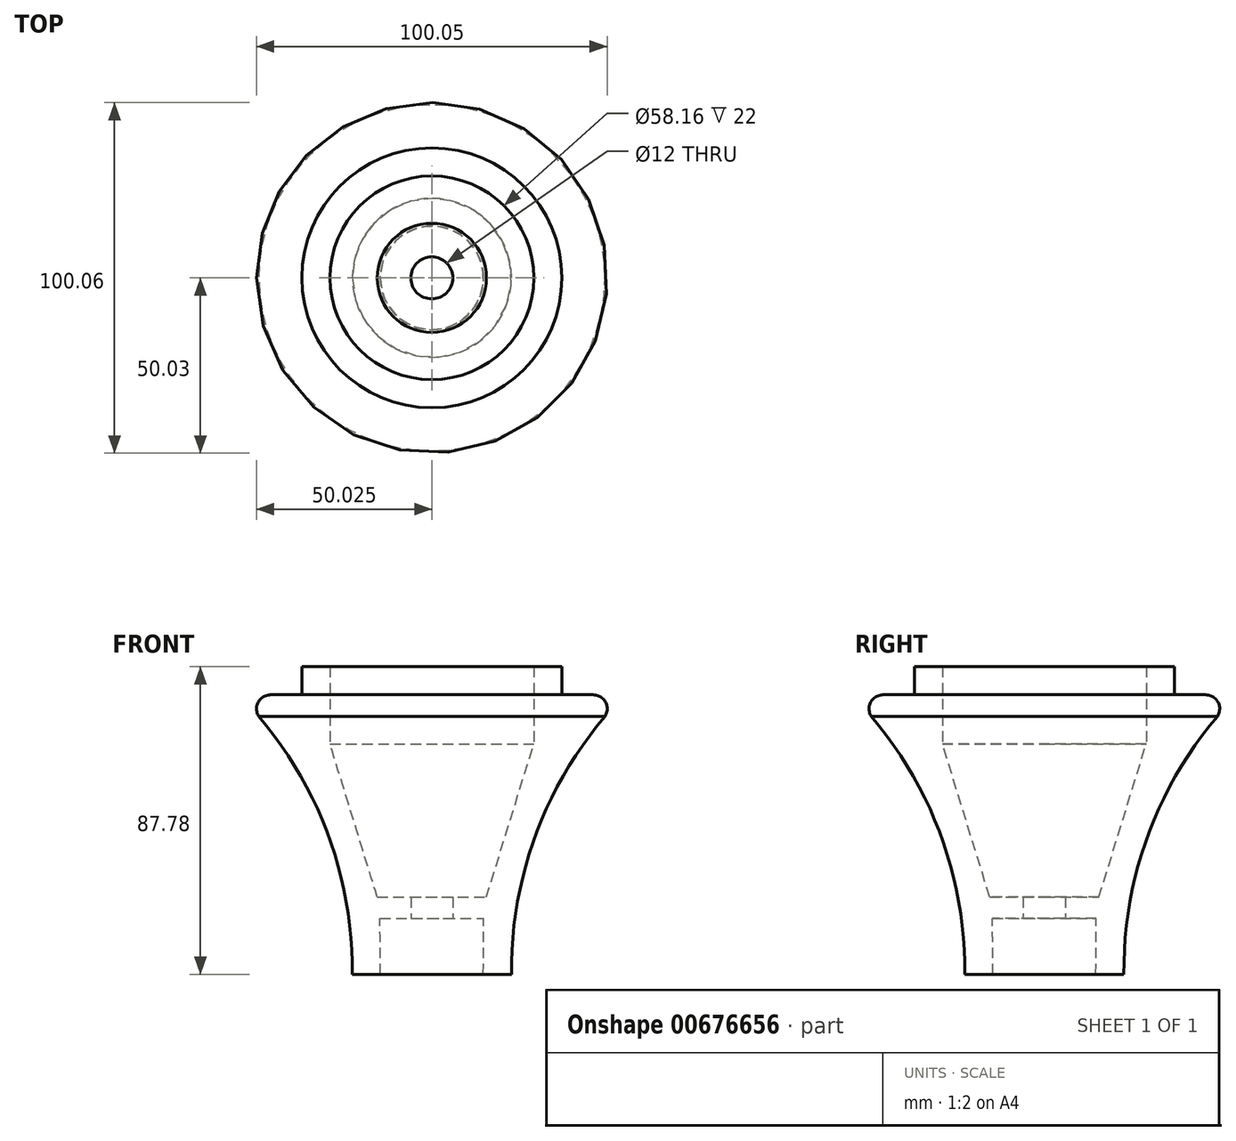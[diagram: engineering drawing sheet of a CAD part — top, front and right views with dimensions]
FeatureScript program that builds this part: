
annotation { "Feature Type Name" : "Feature", "Feature Type Description" : "" }
export const myFeature = defineFeature(function(context is Context, id is Id, definition is map)
    precondition{}
    {
        {
            var Q0;
            Q0=qCreatedBy(makeId("Front.planeOp"),FACE);
            var sketch = newSketch(context, id + "F0", { "sketchPlane" : qUnion([Q0])});
            skCircle(sketch, "E0", {"center": v(0, 0) * mm, "radius": 4 * mm});
            skLineSegment(sketch, "E1", {"start": v(0, 4) * mm, "end": v(-8.95, 4) * mm});
            skLineSegment(sketch, "E2", {"start": v(-8.95, 4) * mm, "end": v(-8.95, 12) * mm});
            skLineSegment(sketch, "E3", {"start": v(-8.95, 12) * mm, "end": v(-16.95, 12) * mm});
            skLineSegment(sketch, "E4", {"start": v(-31.34, -75.78) * mm, "end": v(-23.34, -75.78) * mm});
            skArc(sketch, "E5", {"start": v(3.36, -2.17) * mm, "mid": v(-16.63, -36.56) * mm, "end": v(-23.34, -75.78) * mm});
            skLineSegment(sketch, "E6", {"start": v(-16.95, 12) * mm, "end": v(-16.95, -10) * mm});
            skLineSegment(sketch, "E7", {"start": v(-31.22, -59.78) * mm, "end": v(-46.03, -59.78) * mm});
            skLineSegment(sketch, "E8", {"start": v(-46.03, -59.78) * mm, "end": v(-46.03, -53.78) * mm});
            skLineSegment(sketch, "E9", {"start": v(-46.03, -53.78) * mm, "end": v(-30.46, -53.78) * mm});
            skLineSegment(sketch, "E10", {"start": v(-16.95, -10) * mm, "end": v(-30.46, -53.78) * mm});
            skLineSegment(sketch, "E11", {"start": v(-31.22, -59.78) * mm, "end": v(-31.34, -75.78) * mm});
            skLineSegment(sketch, "E12", {"start": v(-31.34, -75.78) * mm, "end": v(-58.2, -75.56) * mm});
            skLineSegment(sketch, "E13", {"start": v(-58.2, -75.56) * mm, "end": v(-58.2, 12) * mm});
            skLineSegment(sketch, "E14", {"start": v(-58.2, 12) * mm, "end": v(-16.95, 12) * mm});
            skSolve(sketch);
        }
        {
            var Q0;
            {var subQ3=sQuery(id+"F0.wireOp",EDGE,"E1");Q0=makeQuery(id+"F0.imprint","IMPRINT",FACE,{"disambiguationData":[TD([[makeQuery(id+"F0.imprint","IMPRINT",EDGE,{"derivedFrom":subQ3}),1.0]])]});}
            var Q1;
            {var subQ0=sQuery(id+"F0.wireOp",EDGE,"E7");Q1=makeQuery(id+"F0.imprint","IMPRINT",FACE,{"disambiguationData":[TD([[makeQuery(id+"F0.imprint","IMPRINT",EDGE,{"derivedFrom":subQ0}),-1.0]])]});}
            var Q2;
            {var subQ0=sQuery(id+"F0.wireOp",EDGE,"E0");var subQ1=makeQuery(id+"F0.imprint","INTERSECT",VERTEX,{"derivedFrom":[subQ0,sQuery(id+"F0.wireOp",EDGE,"E1")]});Q2=makeQuery(id+"F0.imprint","IMPRINT",FACE,{"disambiguationData":[TD([[makeQuery(id+"F0.imprint","IMPRINT",EDGE,{"disambiguationData":[TD([[subQ1,-1.0]])],"derivedFrom":subQ0}),1.0]])]});}
            var Q3;
            Q3=sQuery(id+"F0.wireOp",EDGE,"E8");
            revolve(context, id + "F1", {"entities" : qUnion([Q0, Q1, Q2]), "axis" : qUnion([Q3]), "revolveType" : RevolveType.FULL});
        }
        {
            var Q0;
            Q0=makeQuery(id+"F1.opRevolve","SWEPT_FACE",FACE,{"disambiguationData":[OSD([sQuery(id+"F0.wireOp",EDGE,"E7")])]});
            var sketch = newSketch(context, id + "F2", { "sketchPlane" : qUnion([Q0])});
            skCircle(sketch, "E15", {"center": v(-46.03, 0) * mm, "radius": 6 * mm});
            skCircle(sketch, "E16", {"center": v(-46.03, 0) * mm, "radius": 14 * mm});
            skSolve(sketch);
        }
        {
            var Q0;
            Q0=sQuery(id+"F2.wireOp",VERTEX,"E15.center");
            var Q1;
            Q1=makeQuery(id+"F1.opRevolve","SWEPT_BODY",BODY,{"disambiguationData":[OSD([sQuery(id+"F0.wireOp",EDGE,"E0"),sQuery(id+"F0.wireOp",EDGE,"E1"),sQuery(id+"F0.wireOp",EDGE,"E2"),sQuery(id+"F0.wireOp",EDGE,"E3"),sQuery(id+"F0.wireOp",EDGE,"E4"),sQuery(id+"F0.wireOp",EDGE,"E5"),sQuery(id+"F0.wireOp",EDGE,"E6"),sQuery(id+"F0.wireOp",EDGE,"E7"),sQuery(id+"F0.wireOp",EDGE,"E8"),sQuery(id+"F0.wireOp",EDGE,"E9"),sQuery(id+"F0.wireOp",EDGE,"E10"),sQuery(id+"F0.wireOp",EDGE,"E11")])]});
            hole(context, id + "F3", {"style" : HoleStyle.SIMPLE, "endStyle" : HoleEndStyle.THROUGH, "holeDiameter" : 12 * mm, "majorDiameter" : 5 * mm, "isTappedThrough" : true, "tappedDepth" : 12 * mm, "tapClearance" : 3, "locations" : qUnion([Q0]), "scope" : qUnion([Q1])});
        }
    });
